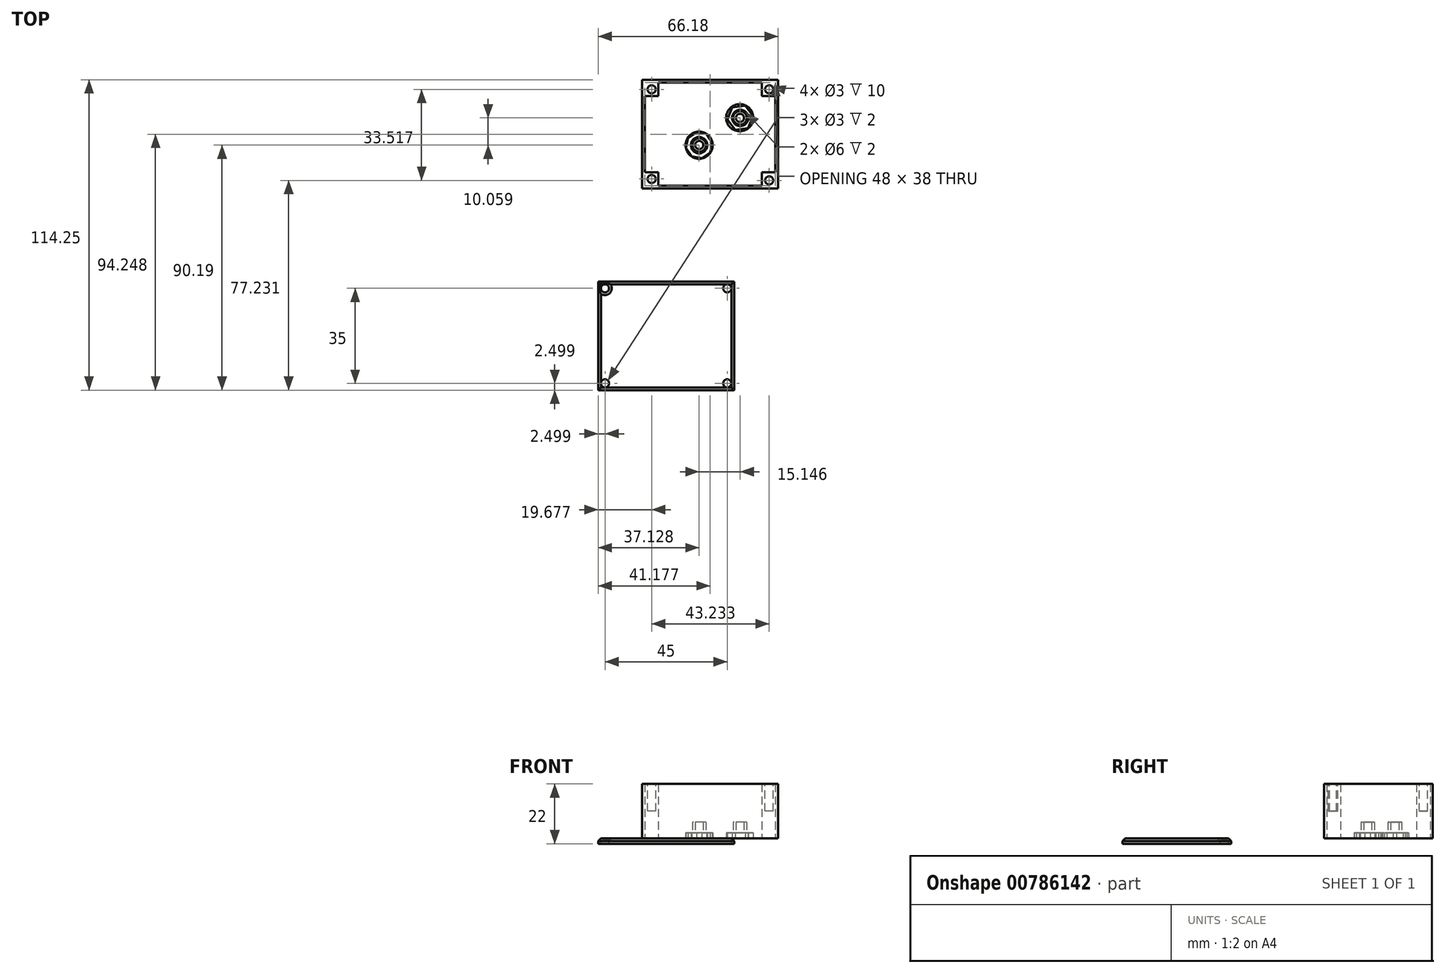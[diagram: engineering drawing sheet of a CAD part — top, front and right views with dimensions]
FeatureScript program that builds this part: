
annotation { "Feature Type Name" : "Feature", "Feature Type Description" : "" }
export const myFeature = defineFeature(function(context is Context, id is Id, definition is map)
    precondition{}
    {
        {
            var Q0;
            Q0=qCreatedBy(makeId("Top.planeOp"),FACE);
            var sketch = newSketch(context, id + "F0", { "sketchPlane" : qUnion([Q0])});
            skLineSegment(sketch, "E0.bottom", {"start": v(-46.73, 54.47) * mm, "end": v(3.27, 54.47) * mm});
            skLineSegment(sketch, "E0.top", {"start": v(-46.73, 14.47) * mm, "end": v(3.27, 14.47) * mm});
            skLineSegment(sketch, "E0.left", {"start": v(-46.73, 54.47) * mm, "end": v(-46.73, 14.47) * mm});
            skLineSegment(sketch, "E0.right", {"start": v(3.27, 54.47) * mm, "end": v(3.27, 14.47) * mm});
            skSolve(sketch);
        }
        {
            var Q0;
            Q0=makeQuery(id+"F0.imprint","IMPRINT",FACE,{"disambiguationData":[TD([[makeQuery(id+"F0.imprint","IMPRINT",EDGE,{"derivedFrom":sQuery(id+"F0.wireOp",EDGE,"E0.bottom")}),-1.0]])]});
            extrude(context, id + "F1", {"entities" : qUnion([Q0]), "depth" : 20 * mm, "offsetDistance" : 25 * mm});
        }
        {
            var Q0;
            Q0=makeQuery(id+"F1.opExtrude","CAP_FACE",FACE,{"disambiguationData":[OSD([sQuery(id+"F0.wireOp",EDGE,"E0.bottom"),sQuery(id+"F0.wireOp",EDGE,"E0.top"),sQuery(id+"F0.wireOp",EDGE,"E0.left"),sQuery(id+"F0.wireOp",EDGE,"E0.right")])],"isStart":false});
            var sketch = newSketch(context, id + "F2", { "sketchPlane" : qUnion([Q0])});
            skLineSegment(sketch, "E1.bottom", {"start": v(2.27, 53.47) * mm, "end": v(-45.73, 53.47) * mm});
            skLineSegment(sketch, "E1.top", {"start": v(2.27, 15.47) * mm, "end": v(-45.73, 15.47) * mm});
            skLineSegment(sketch, "E1.left", {"start": v(2.27, 53.47) * mm, "end": v(2.27, 15.47) * mm});
            skLineSegment(sketch, "E1.right", {"start": v(-45.73, 53.47) * mm, "end": v(-45.73, 15.47) * mm});
            skPoint(sketch, "E1.middle", {"position": v(-21.73, 34.47) * mm});
            skPoint(sketch, "E1.middle.positionSnap0", {"position": v(-21.73, 54.47) * mm});
            skPoint(sketch, "E1.middle.positionSnap1", {"position": v(-46.73, 34.47) * mm});
            skPoint(sketch, "E1.centerSnap0", {"position": v(-21.73, 54.47) * mm});
            skPoint(sketch, "E1.centerSnap1", {"position": v(-46.73, 34.47) * mm});
            skSolve(sketch);
        }
        {
            var Q0;
            Q0=makeQuery(id+"F2.imprint","IMPRINT",FACE,{"disambiguationData":[TD([[makeQuery(id+"F2.imprint","IMPRINT",EDGE,{"derivedFrom":sQuery(id+"F2.wireOp",EDGE,"E1.bottom")}),1.0]])]});
            var Q1;
            Q1 = qSketchRegion(id + "F8", true);
            extrude(context, id + "F3", {"entities" : qUnion([Q0, Q1]), "operationType" : NewBodyOperationType.REMOVE, "oppositeDirection" : true, "depth" : 19 * mm, "offsetDistance" : 25 * mm});
        }
        {
            var Q0;
            Q0=makeQuery(id+"F3.boolean.opBoolean","COPY",FACE,{"derivedFrom":makeQuery(id+"F3.opExtrude","CAP_FACE",FACE,{"disambiguationData":[OSD([sQuery(id+"F2.wireOp",EDGE,"E1.bottom"),sQuery(id+"F2.wireOp",EDGE,"E1.top"),sQuery(id+"F2.wireOp",EDGE,"E1.left"),sQuery(id+"F2.wireOp",EDGE,"E1.right")])],"isStart":false})});
            var sketch = newSketch(context, id + "F4", { "sketchPlane" : qUnion([Q0])});
            skLineSegment(sketch, "E2.bottom", {"start": v(-45.73, 53.47) * mm, "end": v(-40.73, 53.47) * mm});
            skLineSegment(sketch, "E2.top", {"start": v(-45.73, 48.47) * mm, "end": v(-40.73, 48.47) * mm});
            skLineSegment(sketch, "E2.left", {"start": v(-45.73, 53.47) * mm, "end": v(-45.73, 48.47) * mm});
            skLineSegment(sketch, "E2.right", {"start": v(-40.73, 53.47) * mm, "end": v(-40.73, 48.47) * mm});
            skLineSegment(sketch, "E3.bottom", {"start": v(-45.73, 20.47) * mm, "end": v(-40.73, 20.47) * mm});
            skLineSegment(sketch, "E3.top", {"start": v(-45.73, 15.47) * mm, "end": v(-40.73, 15.47) * mm});
            skLineSegment(sketch, "E3.left", {"start": v(-45.73, 20.47) * mm, "end": v(-45.73, 15.47) * mm});
            skLineSegment(sketch, "E3.right", {"start": v(-40.73, 20.47) * mm, "end": v(-40.73, 15.47) * mm});
            skLineSegment(sketch, "E4.bottom", {"start": v(-2.73, 53.47) * mm, "end": v(2.27, 53.47) * mm});
            skLineSegment(sketch, "E4.top", {"start": v(-2.73, 48.47) * mm, "end": v(2.27, 48.47) * mm});
            skLineSegment(sketch, "E4.left", {"start": v(-2.73, 53.47) * mm, "end": v(-2.73, 48.47) * mm});
            skLineSegment(sketch, "E4.right", {"start": v(2.27, 53.47) * mm, "end": v(2.27, 48.47) * mm});
            skLineSegment(sketch, "E5.bottom", {"start": v(2.27, 15.47) * mm, "end": v(-2.73, 15.47) * mm});
            skLineSegment(sketch, "E5.top", {"start": v(2.27, 20.47) * mm, "end": v(-2.73, 20.47) * mm});
            skLineSegment(sketch, "E5.left", {"start": v(2.27, 15.47) * mm, "end": v(2.27, 20.47) * mm});
            skLineSegment(sketch, "E5.right", {"start": v(-2.73, 15.47) * mm, "end": v(-2.73, 20.47) * mm});
            skSolve(sketch);
        }
        {
            var Q0;
            Q0=makeQuery(id+"F4.imprint","IMPRINT",FACE,{"disambiguationData":[TD([[makeQuery(id+"F4.imprint","IMPRINT",EDGE,{"derivedFrom":sQuery(id+"F4.wireOp",EDGE,"E4.bottom")}),1.0]])]});
            var Q1;
            Q1=makeQuery(id+"F4.imprint","IMPRINT",FACE,{"disambiguationData":[TD([[makeQuery(id+"F4.imprint","IMPRINT",EDGE,{"derivedFrom":sQuery(id+"F4.wireOp",EDGE,"E5.bottom")}),-1.0]])]});
            var Q2;
            Q2=makeQuery(id+"F4.imprint","IMPRINT",FACE,{"disambiguationData":[TD([[makeQuery(id+"F4.imprint","IMPRINT",EDGE,{"derivedFrom":sQuery(id+"F4.wireOp",EDGE,"E3.bottom")}),-1.0]])]});
            var Q3;
            Q3=makeQuery(id+"F4.imprint","IMPRINT",FACE,{"disambiguationData":[TD([[makeQuery(id+"F4.imprint","IMPRINT",EDGE,{"derivedFrom":sQuery(id+"F4.wireOp",EDGE,"E2.bottom")}),1.0]])]});
            extrude(context, id + "F5", {"entities" : qUnion([Q0, Q1, Q2, Q3]), "operationType" : NewBodyOperationType.ADD, "depth" : 19 * mm, "offsetDistance" : 25 * mm});
        }
        {
            var Q0;
            Q0=makeQuery(id+"F5.boolean.opBoolean","MERGE",FACE,{"derivedFrom":[makeQuery(id+"F1.opExtrude","CAP_FACE",FACE,{"disambiguationData":[OSD([sQuery(id+"F0.wireOp",EDGE,"E0.bottom"),sQuery(id+"F0.wireOp",EDGE,"E0.top"),sQuery(id+"F0.wireOp",EDGE,"E0.left"),sQuery(id+"F0.wireOp",EDGE,"E0.right")])],"isStart":false}),makeQuery(id+"F5.opExtrude","CAP_FACE",FACE,{"disambiguationData":[OSD([sQuery(id+"F4.wireOp",EDGE,"E2.bottom"),sQuery(id+"F4.wireOp",EDGE,"E2.top"),sQuery(id+"F4.wireOp",EDGE,"E2.left"),sQuery(id+"F4.wireOp",EDGE,"E2.right")])],"isStart":false}),makeQuery(id+"F5.opExtrude","CAP_FACE",FACE,{"disambiguationData":[OSD([sQuery(id+"F4.wireOp",EDGE,"E3.bottom"),sQuery(id+"F4.wireOp",EDGE,"E3.top"),sQuery(id+"F4.wireOp",EDGE,"E3.left"),sQuery(id+"F4.wireOp",EDGE,"E3.right")])],"isStart":false}),makeQuery(id+"F5.opExtrude","CAP_FACE",FACE,{"disambiguationData":[OSD([sQuery(id+"F4.wireOp",EDGE,"E4.bottom"),sQuery(id+"F4.wireOp",EDGE,"E4.top"),sQuery(id+"F4.wireOp",EDGE,"E4.left"),sQuery(id+"F4.wireOp",EDGE,"E4.right")])],"isStart":false}),makeQuery(id+"F5.opExtrude","CAP_FACE",FACE,{"disambiguationData":[OSD([sQuery(id+"F4.wireOp",EDGE,"E5.bottom"),sQuery(id+"F4.wireOp",EDGE,"E5.top"),sQuery(id+"F4.wireOp",EDGE,"E5.left"),sQuery(id+"F4.wireOp",EDGE,"E5.right")])],"isStart":false})]});
            var sketch = newSketch(context, id + "F6", { "sketchPlane" : qUnion([Q0])});
            skCircle(sketch, "E6", {"center": v(-43.23, 50.97) * mm, "radius": 1.5 * mm});
            skPoint(sketch, "E6.centerSnap0", {"position": v(-43.23, 48.47) * mm});
            skPoint(sketch, "E6.centerSnap1", {"position": v(-40.73, 50.97) * mm});
            skCircle(sketch, "E7", {"center": v(-43.23, 17.97) * mm, "radius": 1.5 * mm});
            skPoint(sketch, "E7.centerSnap0", {"position": v(-43.23, 20.47) * mm});
            skPoint(sketch, "E7.centerSnap1", {"position": v(-40.73, 17.97) * mm});
            skCircle(sketch, "E8", {"center": v(0, 50.97) * mm, "radius": 1.5 * mm});
            skPoint(sketch, "E8.centerSnap0", {"position": v(-2.73, 50.97) * mm});
            skPoint(sketch, "E9.centerSnap0", {"position": v(-2.73, 17.58) * mm});
            skPoint(sketch, "E10.centerSnap0", {"position": v(-2.73, 17.97) * mm});
            skCircle(sketch, "E11", {"center": v(0, 17.45) * mm, "radius": 1.5 * mm});
            skSolve(sketch);
        }
        {
            var Q0;
            Q0=makeQuery(id+"F6.imprint","IMPRINT",FACE,{"disambiguationData":[TD([[makeQuery(id+"F6.imprint","IMPRINT",EDGE,{"derivedFrom":sQuery(id+"F6.wireOp",EDGE,"E6")}),1.0]])]});
            var Q1;
            Q1=makeQuery(id+"F6.imprint","IMPRINT",FACE,{"disambiguationData":[TD([[makeQuery(id+"F6.imprint","IMPRINT",EDGE,{"derivedFrom":sQuery(id+"F6.wireOp",EDGE,"E8")}),1.0]])]});
            var Q2;
            Q2=makeQuery(id+"F6.imprint","IMPRINT",FACE,{"disambiguationData":[TD([[makeQuery(id+"F6.imprint","IMPRINT",EDGE,{"derivedFrom":sQuery(id+"F6.wireOp",EDGE,"E7")}),1.0]])]});
            var Q3;
            Q3=makeQuery(id+"F6.imprint","IMPRINT",FACE,{"disambiguationData":[TD([[makeQuery(id+"F6.imprint","IMPRINT",EDGE,{"derivedFrom":sQuery(id+"F6.wireOp",EDGE,"E11")}),1.0]])]});
            extrude(context, id + "F7", {"entities" : qUnion([Q0, Q1, Q2, Q3]), "operationType" : NewBodyOperationType.REMOVE, "oppositeDirection" : true, "depth" : 10 * mm, "hasOffset" : true, "offsetDistance" : 10 * mm});
        }
        {
            var Q0;
            Q0=makeQuery(id+"F3.boolean.opBoolean","COPY",FACE,{"derivedFrom":makeQuery(id+"F3.opExtrude","CAP_FACE",FACE,{"disambiguationData":[OSD([sQuery(id+"F2.wireOp",EDGE,"E1.bottom"),sQuery(id+"F2.wireOp",EDGE,"E1.top"),sQuery(id+"F2.wireOp",EDGE,"E1.left"),sQuery(id+"F2.wireOp",EDGE,"E1.right")])],"isStart":false})});
            var sketch = newSketch(context, id + "F8", { "sketchPlane" : qUnion([Q0])});
            skCircle(sketch, "E12", {"center": v(-25.73, 30.47) * mm, "radius": 2.5 * mm});
            skCircle(sketch, "E13", {"center": v(-10.73, 40.47) * mm, "radius": 2.5 * mm});
            skCircle(sketch, "E14", {"center": v(-10.73, 40.47) * mm, "radius": 1.5 * mm});
            skCircle(sketch, "E15", {"center": v(-25.73, 30.47) * mm, "radius": 1.5 * mm});
            skSolve(sketch);
        }
        {
            var Q0;
            Q0 = qSketchRegion(id + "F8", true);
            extrude(context, id + "F9", {"entities" : qUnion([Q0]), "operationType" : NewBodyOperationType.ADD, "depth" : 5 * mm, "offsetDistance" : 25 * mm});
        }
        {
            var Q0;
            {var subQ0=sQuery(id+"F2.wireOp",EDGE,"E1.bottom");var subQ1=sQuery(id+"F2.wireOp",EDGE,"E1.top");var subQ2=sQuery(id+"F2.wireOp",EDGE,"E1.left");var subQ3=sQuery(id+"F2.wireOp",EDGE,"E1.right");Q0=makeQuery(id+"F9.boolean.opBoolean","SPLIT",FACE,{"disambiguationData":[TD([makeQuery(id+"F3.boolean.opBoolean","COPY",FACE,{"derivedFrom":makeQuery(id+"F3.opExtrude","SWEPT_FACE",FACE,{"disambiguationData":[OSD([subQ0])]})})])],"derivedFrom":makeQuery(id+"F3.boolean.opBoolean","COPY",FACE,{"derivedFrom":makeQuery(id+"F3.opExtrude","CAP_FACE",FACE,{"disambiguationData":[OSD([subQ0,subQ1,subQ2,subQ3])],"isStart":false})})});}
            extrude(context, id + "F10", {"entities" : qUnion([Q0]), "operationType" : NewBodyOperationType.REMOVE, "oppositeDirection" : true, "depth" : 2 * mm, "offsetDistance" : 25 * mm});
        }
        {
            var Q0;
            Q0=qCreatedBy(makeId("Top.planeOp"),FACE);
            var sketch = newSketch(context, id + "F11", { "sketchPlane" : qUnion([Q0])});
            skCircle(sketch, "E16", {"center": v(-25.78, 30.4) * mm, "radius": 5 * mm});
            skCircle(sketch, "E17", {"center": v(-10.83, 40.52) * mm, "radius": 5 * mm});
            skSolve(sketch);
        }
        {
            var Q0;
            Q0=makeQuery(id+"F11.imprint","IMPRINT",FACE,{"disambiguationData":[TD([[makeQuery(id+"F11.imprint","IMPRINT",EDGE,{"derivedFrom":sQuery(id+"F11.wireOp",EDGE,"E16")}),1.0]])]});
            var Q1;
            Q1=makeQuery(id+"F11.imprint","IMPRINT",FACE,{"disambiguationData":[TD([[makeQuery(id+"F11.imprint","IMPRINT",EDGE,{"derivedFrom":sQuery(id+"F11.wireOp",EDGE,"E17")}),1.0]])]});
            extrude(context, id + "F12", {"entities" : qUnion([Q0, Q1]), "operationType" : NewBodyOperationType.ADD, "depth" : 2 * mm, "offsetDistance" : 25 * mm});
        }
        {
            var Q0;
            {var subQ3=sQuery(id+"F0.wireOp",EDGE,"E0.right");var subQ5=sQuery(id+"F0.wireOp",EDGE,"E0.top");var subQ8=sQuery(id+"F0.wireOp",EDGE,"E0.left");var subQ12=sQuery(id+"F0.wireOp",EDGE,"E0.bottom");Q0=makeQuery(id+"F10.boolean.opBoolean","SPLIT",FACE,{"disambiguationData":[TD([makeQuery(id+"F1.opExtrude","SWEPT_FACE",FACE,{"disambiguationData":[OSD([subQ12])]})])],"derivedFrom":makeQuery(id+"F1.opExtrude","CAP_FACE",FACE,{"disambiguationData":[OSD([subQ12,subQ5,subQ8,subQ3])],"isStart":true})});}
            var sketch = newSketch(context, id + "F13", { "sketchPlane" : qUnion([Q0])});
            skCircle(sketch, "E18", {"center": v(-25.78, -30.4) * mm, "radius": 3 * mm});
            skCircle(sketch, "E19", {"center": v(-10.64, -40.47) * mm, "radius": 3 * mm});
            skCircle(sketch, "E20.cCircle", {"center": v(-25.78, -30.4) * mm, "radius": 4.51 * mm, "construction": true});
            skLineSegment(sketch, "E20.0", {"start": v(-26.74, -35.2) * mm, "end": v(-29.85, -33.12) * mm});
            skLineSegment(sketch, "E20.1", {"start": v(-29.85, -33.12) * mm, "end": v(-30.57, -29.45) * mm});
            skLineSegment(sketch, "E20.2", {"start": v(-30.57, -29.45) * mm, "end": v(-28.49, -26.35) * mm});
            skLineSegment(sketch, "E20.3", {"start": v(-28.49, -26.35) * mm, "end": v(-24.82, -25.62) * mm});
            skLineSegment(sketch, "E20.4", {"start": v(-24.82, -25.62) * mm, "end": v(-21.72, -27.7) * mm});
            skLineSegment(sketch, "E20.5", {"start": v(-21.72, -27.7) * mm, "end": v(-21, -31.37) * mm});
            skLineSegment(sketch, "E20.6", {"start": v(-21, -31.37) * mm, "end": v(-23.07, -34.47) * mm});
            skLineSegment(sketch, "E20.7", {"start": v(-23.07, -34.47) * mm, "end": v(-26.74, -35.2) * mm});
            skPoint(sketch, "E20.0.midPoint", {"position": v(-28.3, -34.16) * mm});
            skCircle(sketch, "E21.cCircle", {"center": v(-10.64, -40.47) * mm, "radius": 4.14 * mm, "construction": true});
            skLineSegment(sketch, "E21.0", {"start": v(-8.81, -44.9) * mm, "end": v(-13.55, -44.26) * mm});
            skLineSegment(sketch, "E21.1", {"start": v(-13.55, -44.26) * mm, "end": v(-15.38, -39.84) * mm});
            skLineSegment(sketch, "E21.2", {"start": v(-15.38, -39.84) * mm, "end": v(-12.46, -36.05) * mm});
            skLineSegment(sketch, "E21.3", {"start": v(-12.46, -36.05) * mm, "end": v(-7.72, -36.68) * mm});
            skLineSegment(sketch, "E21.4", {"start": v(-7.72, -36.68) * mm, "end": v(-5.9, -41.1) * mm});
            skLineSegment(sketch, "E21.5", {"start": v(-5.9, -41.1) * mm, "end": v(-8.81, -44.9) * mm});
            skPoint(sketch, "E21.0.midPoint", {"position": v(-11.18, -44.58) * mm});
            skSolve(sketch);
        }
        {
            var Q0;
            Q0=makeQuery(id+"F13.imprint","IMPRINT",FACE,{"disambiguationData":[TD([[makeQuery(id+"F13.imprint","IMPRINT",EDGE,{"derivedFrom":sQuery(id+"F13.wireOp",EDGE,"E19")}),-1.0]])]});
            var Q1;
            Q1=makeQuery(id+"F13.imprint","IMPRINT",FACE,{"disambiguationData":[TD([[makeQuery(id+"F13.imprint","IMPRINT",EDGE,{"derivedFrom":sQuery(id+"F13.wireOp",EDGE,"E18")}),-1.0]])]});
            extrude(context, id + "F14", {"entities" : qUnion([Q0, Q1]), "oppositeDirection" : true, "depth" : 2 * mm, "offsetDistance" : 25 * mm});
        }
        {
            var Q0;
            Q0=qCreatedBy(makeId("Top.planeOp"),FACE);
            var sketch = newSketch(context, id + "F15", { "sketchPlane" : qUnion([Q0])});
            skLineSegment(sketch, "E22.bottom", {"start": v(-62.91, -19.78) * mm, "end": v(-12.91, -19.78) * mm});
            skLineSegment(sketch, "E22.top", {"start": v(-62.91, -59.78) * mm, "end": v(-12.91, -59.78) * mm});
            skLineSegment(sketch, "E22.left", {"start": v(-62.91, -19.78) * mm, "end": v(-62.91, -59.78) * mm});
            skLineSegment(sketch, "E22.right", {"start": v(-12.91, -19.78) * mm, "end": v(-12.91, -59.78) * mm});
            skLineSegment(sketch, "E23.left", {"start": v(-18.31, -3.26) * mm, "end": v(-18.31, 0.34) * mm});
            skLineSegment(sketch, "E23.right", {"start": v(-32.5, -3.26) * mm, "end": v(-32.5, 0.34) * mm});
            skCircle(sketch, "E24", {"center": v(-60.41, -22.28) * mm, "radius": 1.5 * mm});
            skCircle(sketch, "E25", {"center": v(-15.41, -22.28) * mm, "radius": 1.5 * mm});
            skCircle(sketch, "E26", {"center": v(-60.41, -57.28) * mm, "radius": 1.5 * mm});
            skCircle(sketch, "E27", {"center": v(-15.41, -57.28) * mm, "radius": 1.5 * mm});
            skSolve(sketch);
        }
        {
            var Q0;
            Q0=makeQuery(id+"F15.imprint","IMPRINT",FACE,{"disambiguationData":[TD([[makeQuery(id+"F15.imprint","IMPRINT",EDGE,{"derivedFrom":sQuery(id+"F15.wireOp",EDGE,"E22.bottom")}),-1.0]])]});
            extrude(context, id + "F16", {"entities" : qUnion([Q0]), "oppositeDirection" : true, "depth" : 2 * mm, "offsetDistance" : 25 * mm});
        }
        {
            var Q0;
            Q0=makeQuery(id+"F16.opExtrude","CAP_EDGE",EDGE,{"disambiguationData":[OSD([sQuery(id+"F15.wireOp",EDGE,"E22.top")])],"isStart":true});
            var Q1;
            Q1=makeQuery(id+"F16.opExtrude","CAP_EDGE",EDGE,{"disambiguationData":[OSD([sQuery(id+"F15.wireOp",EDGE,"E22.right")])],"isStart":true});
            var Q2;
            Q2=makeQuery(id+"F16.opExtrude","CAP_EDGE",EDGE,{"disambiguationData":[OSD([sQuery(id+"F15.wireOp",EDGE,"E22.bottom")])],"isStart":true});
            var Q3;
            Q3=makeQuery(id+"F16.opExtrude","CAP_EDGE",EDGE,{"disambiguationData":[OSD([sQuery(id+"F15.wireOp",EDGE,"E22.left")])],"isStart":true});
            var Q4;
            Q4=makeQuery(id+"F16.opExtrude","CAP_EDGE",EDGE,{"disambiguationData":[OSD([sQuery(id+"F15.wireOp",EDGE,"E24")])],"isStart":true});
            chamfer(context, id + "F17", {"entities" : qUnion([Q0, Q1, Q2, Q3, Q4]), "width" : 1 * mm, "tangentPropagation" : true});
        }
    });
